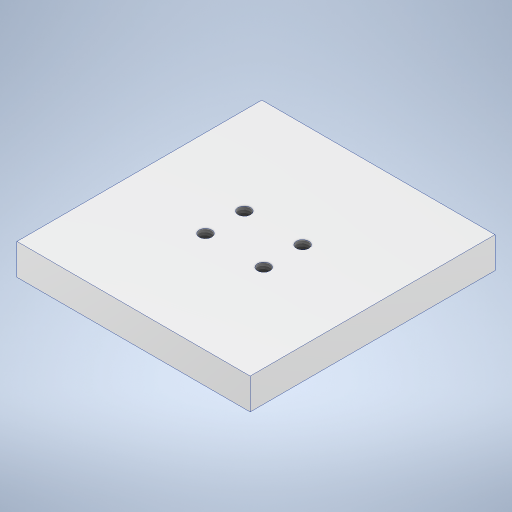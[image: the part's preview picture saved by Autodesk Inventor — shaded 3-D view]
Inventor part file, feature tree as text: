
AUTODESK INVENTOR PART (.ipt)
format: ipt  version: 2023 (Build 270158000, 158)  size: 233,984 bytes
history: native  units: mm
features: sketch x2, extrude x1, hole x1
ambient origin geometry x8: Origin, YZ Plane, XZ Plane, XY Plane, X Axis, Y Axis, Z Axis, Center Point
bodies: Solid1 (feature_tree)
feature tree (4):
  extrude  "Extrusion1"  Depth=63.0mm
  hole  "Furo1"  [1 undecoded]
  sketch  "Sketch1"  dims[d0=60.0mm d1=63.0mm]
  sketch  "Esboço2"  dims[d2=8.0mm d3=0.0mm d5=0.0mm d6=15.0mm d7=0.0mm d8=15.0mm d9=10.0mm d10=0.0mm d11=60.0mm d12=22.5mm d13=3.242mm d14=8.0mm d15=4.0mm d16=2.0mm d17=90.0deg d18=0.5mm d19=20.594885mm d20=26.0mm]
note: 1 required parameter value undecoded (feature->parameter linkage not recoverable at this tier; creation-order binding heuristic only, values carry confidence <= 0.55)
